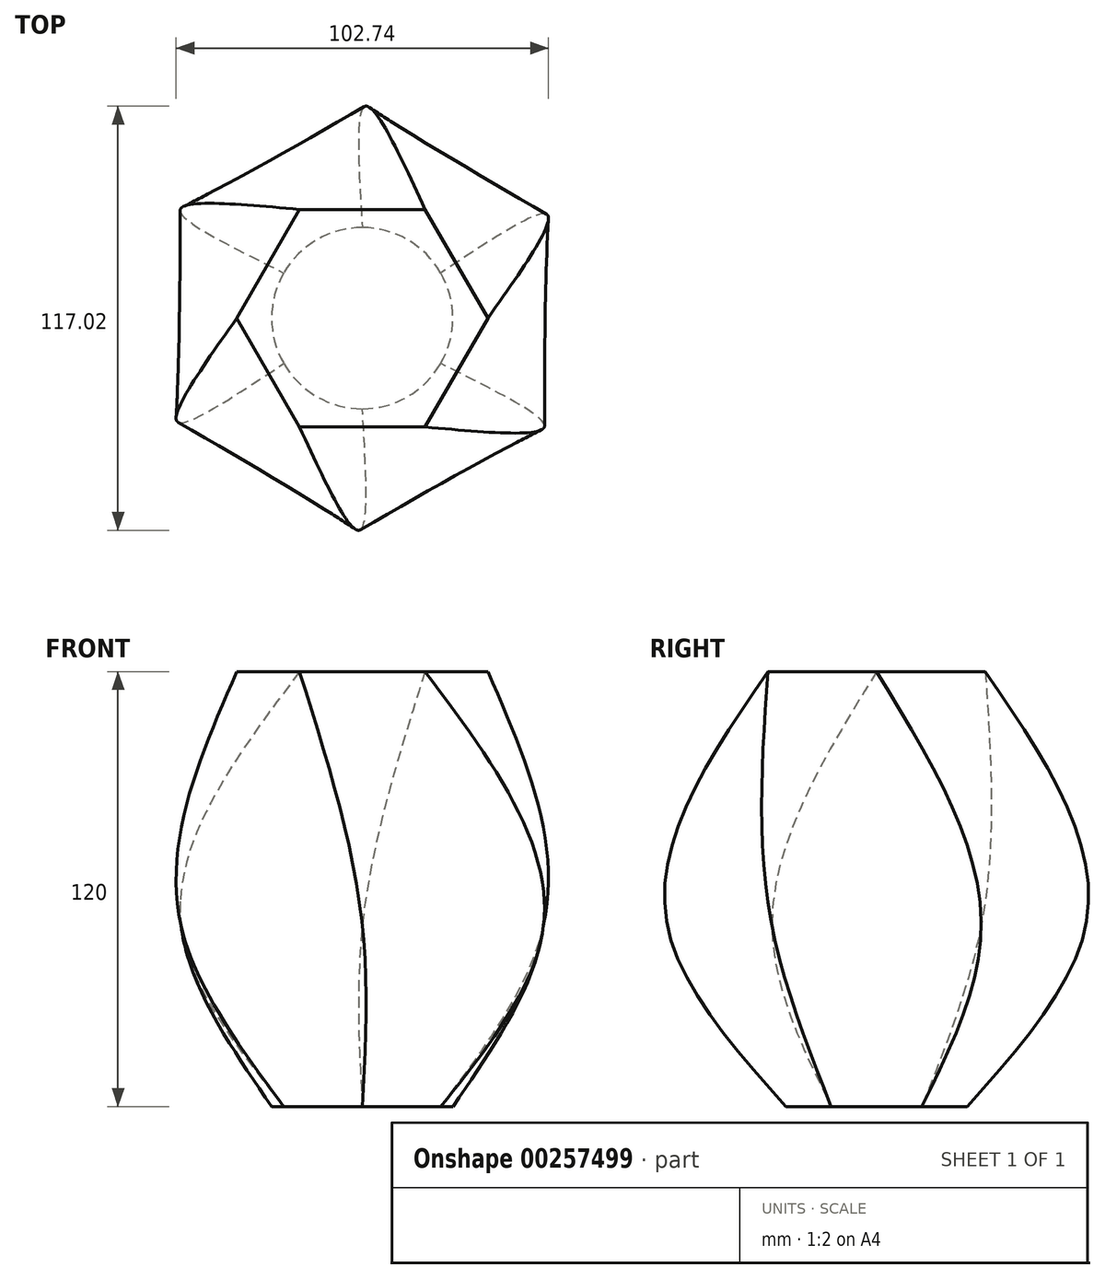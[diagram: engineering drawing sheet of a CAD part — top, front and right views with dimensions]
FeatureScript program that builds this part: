
annotation { "Feature Type Name" : "Feature", "Feature Type Description" : "" }
export const myFeature = defineFeature(function(context is Context, id is Id, definition is map)
    precondition{}
    {
        {
            var Q0;
            Q0=qCreatedBy(makeId("Top.planeOp"),FACE);
            var sketch = newSketch(context, id + "F0", { "sketchPlane" : qUnion([Q0])});
            skCircle(sketch, "E0.cCircle", {"center": v(0, 0) * mm, "radius": 30 * mm, "construction": true});
            skLineSegment(sketch, "E0.0", {"start": v(17.32, -30) * mm, "end": v(-17.32, -30) * mm});
            skLineSegment(sketch, "E0.1", {"start": v(-17.32, -30) * mm, "end": v(-34.64, 0) * mm});
            skLineSegment(sketch, "E0.2", {"start": v(-34.64, 0) * mm, "end": v(-17.32, 30) * mm});
            skLineSegment(sketch, "E0.3", {"start": v(-17.32, 30) * mm, "end": v(17.32, 30) * mm});
            skLineSegment(sketch, "E0.4", {"start": v(17.32, 30) * mm, "end": v(34.64, 0) * mm});
            skLineSegment(sketch, "E0.5", {"start": v(34.64, 0) * mm, "end": v(17.32, -30) * mm});
            skPoint(sketch, "E0.0.midPoint", {"position": v(0, -30) * mm});
            skSolve(sketch);
        }
        {
            var Q0;
            Q0=qCreatedBy(makeId("Top.planeOp"),FACE);
            cPlane(context, id + "F1", {"entities" : qUnion([Q0]), "cplaneType" : CPlaneType.OFFSET, "offset" : 70 * mm, "oppositeDirection" : true, "width" : 150 * mm, "height" : 150 * mm});
        }
        {
            var Q0;
            Q0=qCreatedBy(id+"F1.planeOp",FACE);
            var Q1;
            Q1 = qBodyType(qCreatedBy(id + "F3" ,EDGE), BodyType.WIRE);
            cPlane(context, id + "F2", {"entities" : qUnion([Q0, Q1]), "cplaneType" : CPlaneType.OFFSET, "offset" : 50 * mm, "oppositeDirection" : true, "width" : 150 * mm, "height" : 150 * mm});
        }
        {
            var Q0;
            Q0=qCreatedBy(id+"F1.planeOp",FACE);
            var sketch = newSketch(context, id + "F3", { "sketchPlane" : qUnion([Q0])});
            skCircle(sketch, "E1.cCircle", {"center": v(0, 0) * mm, "radius": 50 * mm, "construction": true});
            skLineSegment(sketch, "E1.0", {"start": v(-50, 28.87) * mm, "end": v(0, 57.74) * mm});
            skLineSegment(sketch, "E1.1", {"start": v(0, 57.74) * mm, "end": v(50, 28.87) * mm});
            skLineSegment(sketch, "E1.2", {"start": v(50, 28.87) * mm, "end": v(50, -28.87) * mm});
            skLineSegment(sketch, "E1.3", {"start": v(50, -28.87) * mm, "end": v(0, -57.74) * mm});
            skLineSegment(sketch, "E1.4", {"start": v(0, -57.74) * mm, "end": v(-50, -28.87) * mm});
            skLineSegment(sketch, "E1.5", {"start": v(-50, -28.87) * mm, "end": v(-50, 28.87) * mm});
            skPoint(sketch, "E1.0.midPoint", {"position": v(-25, 43.3) * mm});
            skSolve(sketch);
        }
        {
            var Q0;
            Q0=qCreatedBy(id+"F2.planeOp",FACE);
            var sketch = newSketch(context, id + "F4", { "sketchPlane" : qUnion([Q0])});
            skCircle(sketch, "E2", {"center": v(0, 0) * mm, "radius": 25 * mm});
            skSolve(sketch);
        }
        {
            var Q0;
            Q0=makeQuery(id+"F0.imprint","IMPRINT",FACE,{"disambiguationData":[TD([[makeQuery(id+"F0.imprint","IMPRINT",EDGE,{"derivedFrom":sQuery(id+"F0.wireOp",EDGE,"E0.0")}),-1.0]])]});
            var Q1;
            Q1=makeQuery(id+"F3.imprint","IMPRINT",FACE,{"disambiguationData":[TD([[makeQuery(id+"F3.imprint","IMPRINT",EDGE,{"derivedFrom":sQuery(id+"F3.wireOp",EDGE,"E1.0")}),-1.0]])]});
            var Q2;
            Q2=makeQuery(id+"F4.imprint","IMPRINT",FACE,{"disambiguationData":[TD([[makeQuery(id+"F4.imprint","IMPRINT",EDGE,{"derivedFrom":sQuery(id+"F4.wireOp",EDGE,"E2")}),1.0]])]});
            loft(context, id + "F5", {"sheetProfilesArray" : [{ "sheetProfileEntities" : qUnion([Q0]) }, { "sheetProfileEntities" : qUnion([Q1]) }, { "sheetProfileEntities" : qUnion([Q2]) }]});
        }
    });
